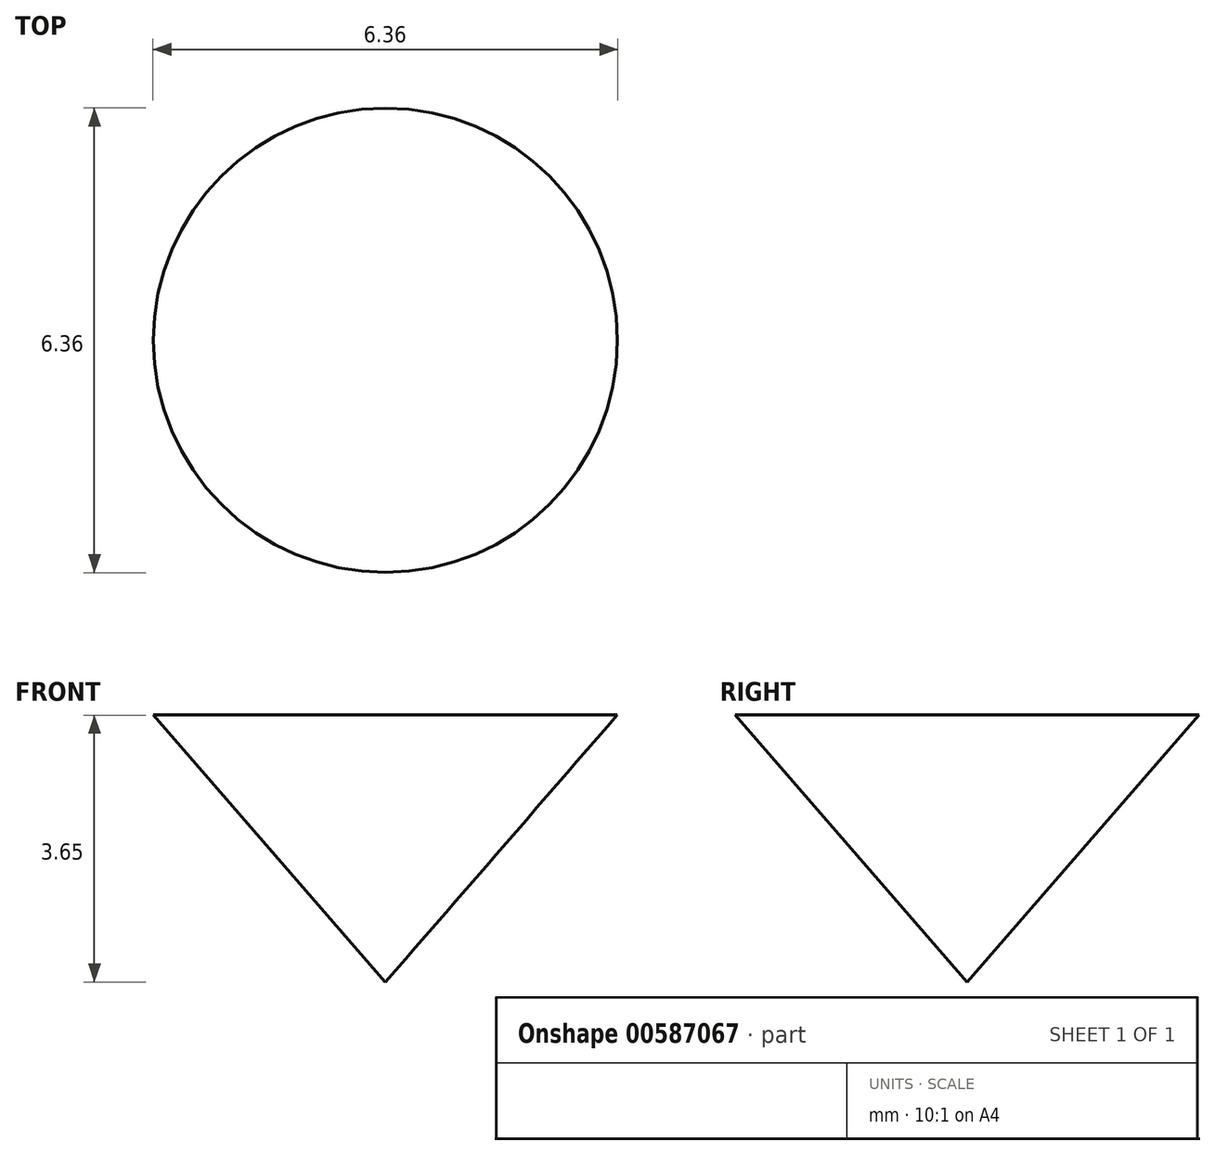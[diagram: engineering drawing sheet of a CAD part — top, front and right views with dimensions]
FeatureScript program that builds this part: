
annotation { "Feature Type Name" : "Feature", "Feature Type Description" : "" }
export const myFeature = defineFeature(function(context is Context, id is Id, definition is map)
    precondition{}
    {
        {
            var Q0;
            Q0=qCreatedBy(makeId("Front.planeOp"),FACE);
            var sketch = newSketch(context, id + "F0", { "sketchPlane" : qUnion([Q0])});
            skLineSegment(sketch, "E0", {"start": v(0, 0) * mm, "end": v(0, 3.65) * mm});
            skLineSegment(sketch, "E1", {"start": v(0, 3.65) * mm, "end": v(0, 3.65) * mm});
            skLineSegment(sketch, "E2", {"start": v(0, 3.65) * mm, "end": v(3.18, 3.65) * mm});
            skLineSegment(sketch, "E3", {"start": v(3.18, 3.65) * mm, "end": v(0, 0) * mm});
            skSolve(sketch);
        }
        {
            var Q0;
            Q0=makeQuery(id+"F0.imprint","IMPRINT",FACE,{"disambiguationData":[TD([[makeQuery(id+"F0.imprint","IMPRINT",EDGE,{"derivedFrom":sQuery(id+"F0.wireOp",EDGE,"E0")}),-1.0]])]});
            var Q1;
            Q1=sQuery(id+"F0.wireOp",EDGE,"E0");
            revolve(context, id + "F1", {"entities" : qUnion([Q0]), "axis" : qUnion([Q1]), "revolveType" : RevolveType.FULL});
        }
    });
